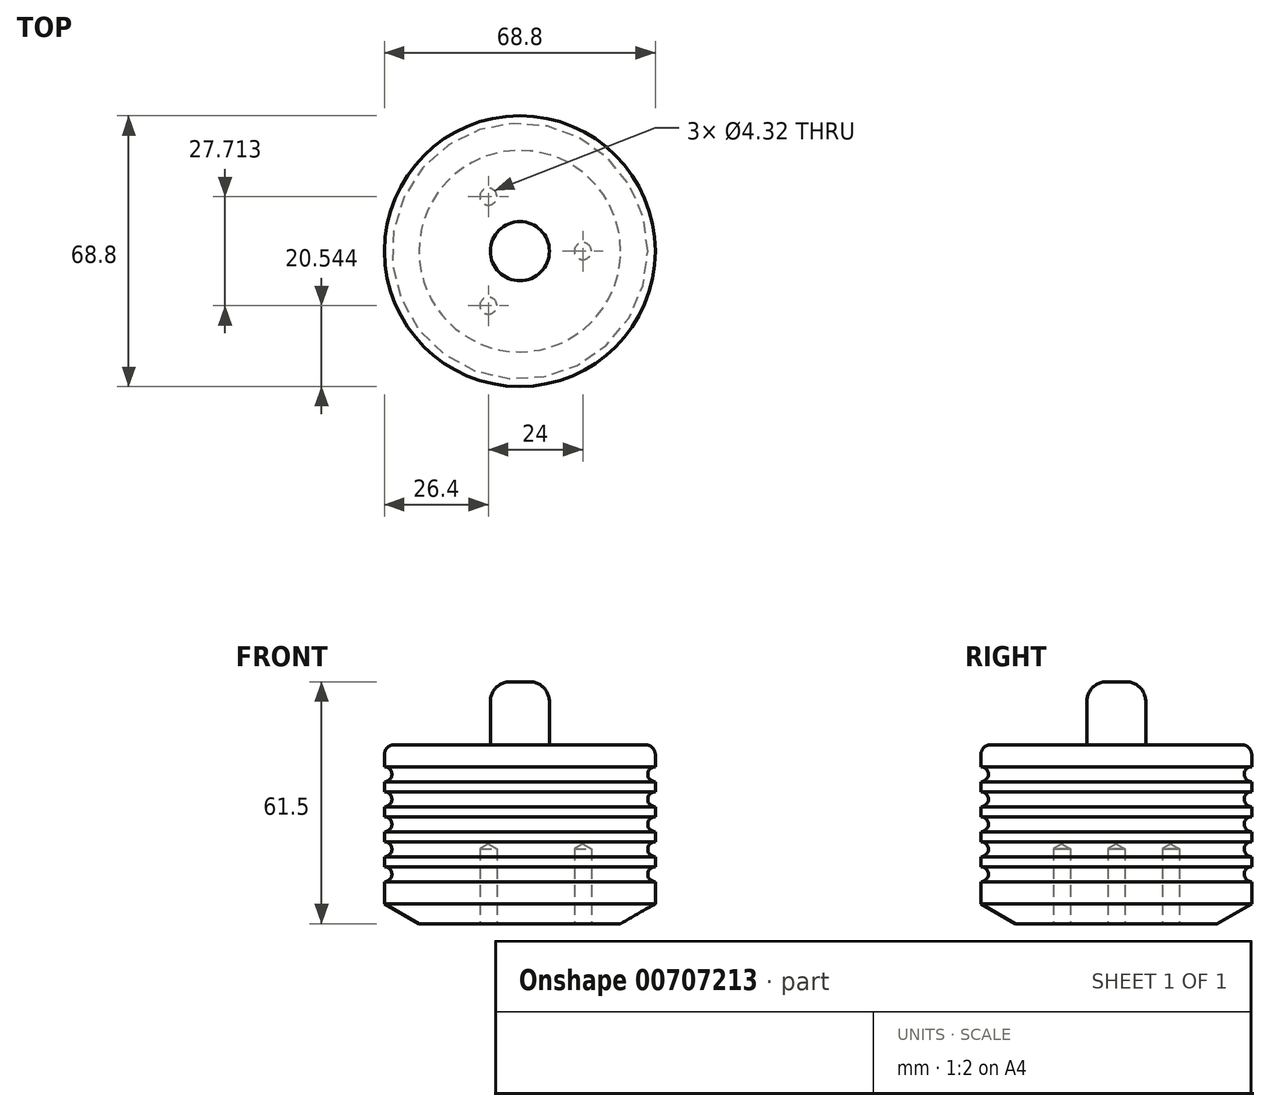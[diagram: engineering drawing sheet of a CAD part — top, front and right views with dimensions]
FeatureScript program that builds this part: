
annotation { "Feature Type Name" : "Feature", "Feature Type Description" : "" }
export const myFeature = defineFeature(function(context is Context, id is Id, definition is map)
    precondition{}
    {
        {
            var Q0;
            Q0=qCreatedBy(makeId("Top.planeOp"),FACE);
            var sketch = newSketch(context, id + "F0", { "sketchPlane" : qUnion([Q0])});
            skCircle(sketch, "E0", {"center": v(0, 0) * mm, "radius": 34.4 * mm});
            skSolve(sketch);
        }
        {
            var Q0;
            Q0 = qSketchRegion(id + "F0", true);
            extrude(context, id + "F1", {"entities" : qUnion([Q0]), "depth" : 45.5 * mm, "offsetDistance" : 25.4 * mm});
        }
        {
            var Q0;
            Q0=makeQuery(id+"F1.opExtrude","CAP_FACE",FACE,{"disambiguationData":[OSD([sQuery(id+"F0.wireOp",EDGE,"E0")])],"isStart":false});
            var sketch = newSketch(context, id + "F2", { "sketchPlane" : qUnion([Q0])});
            skCircle(sketch, "E1", {"center": v(0, 0) * mm, "radius": 7.5 * mm});
            skSolve(sketch);
        }
        {
            var Q0;
            Q0 = qSketchRegion(id + "F2", true);
            extrude(context, id + "F3", {"entities" : qUnion([Q0]), "operationType" : NewBodyOperationType.ADD, "depth" : 16 * mm, "offsetDistance" : 25.4 * mm});
        }
        {
            var Q0;
            Q0=makeQuery(id+"F1.opExtrude","CAP_FACE",FACE,{"disambiguationData":[OSD([sQuery(id+"F0.wireOp",EDGE,"E0")])],"isStart":true});
            var sketch = newSketch(context, id + "F4", { "sketchPlane" : qUnion([Q0])});
            skCircle(sketch, "E2", {"center": v(0, 0) * mm, "radius": 16 * mm});
            skLineSegment(sketch, "E3", {"start": v(0, 0) * mm, "end": v(16, 0) * mm});
            skLineSegment(sketch, "E4", {"start": v(0, 0) * mm, "end": v(-8, 13.86) * mm});
            skLineSegment(sketch, "E5.MirrorCS", {"start": v(0, 0) * mm, "end": v(-8, -13.86) * mm});
            skSolve(sketch);
        }
        {
            var Q0;
            Q0=sQuery(id+"F4.wireOp",VERTEX,"E4.end");
            var Q1;
            Q1=sQuery(id+"F4.wireOp",VERTEX,"E3.end");
            var Q2;
            Q2=sQuery(id+"F4.wireOp",VERTEX,"E5.MirrorCS.end");
            var Q3;
            Q3=makeQuery(id+"F1.opExtrude","SWEPT_BODY",BODY,{"disambiguationData":[OSD([sQuery(id+"F0.wireOp",EDGE,"E0")])]});
            hole(context, id + "F5", {"style" : HoleStyle.SIMPLE, "endStyle" : HoleEndStyle.BLIND, "standardTappedOrClearance" : lookupTablePath({ "standard" : "ANSI", "fit" : "Close", "size" : "#8", "type" : "Clearance" }), "standardBlindInLast" : lookupTablePath({ "fit" : "Close", "standard" : "ANSI", "size" : "#8", "type" : "Clearance" }), "holeDiameter" : 4.32 * mm, "majorDiameter" : 6.35 * mm, "holeDepth" : 19.05 * mm, "isTappedThrough" : true, "tappedDepth" : 12.7 * mm, "tapClearance" : 3, "locations" : qUnion([Q0, Q1, Q2]), "scope" : qUnion([Q3])});
        }
        {
            var Q0;
            Q0=makeQuery(id+"F1.opExtrude","CAP_EDGE",EDGE,{"disambiguationData":[OSD([sQuery(id+"F0.wireOp",EDGE,"E0")])],"isStart":true});
            chamfer(context, id + "F6", {"entities" : qUnion([Q0]), "chamferType" : ChamferType.OFFSET_ANGLE, "width" : 5.08 * mm, "oppositeDirection" : false, "angle" : 60 * degree, "tangentPropagation" : true});
        }
        {
            var Q0;
            Q0=qCreatedBy(makeId("Right.planeOp"),FACE);
            var sketch = newSketch(context, id + "F7", { "sketchPlane" : qUnion([Q0])});
            skLineSegment(sketch, "E6", {"start": v(0, 0) * mm, "end": v(0, 5.08) * mm});
            skLineSegment(sketch, "E7", {"start": v(0, 5.08) * mm, "end": v(-34.4, 5.08) * mm});
            skLineSegment(sketch, "E8", {"start": v(-34.4, 5.08) * mm, "end": v(-34.4, 45.5) * mm});
            skLineSegment(sketch, "E9", {"start": v(-34.4, 25.29) * mm, "end": v(-39.91, 25.29) * mm});
            skCircle(sketch, "E10", {"center": v(-34.4, 25.29) * mm, "radius": 1.9 * mm});
            skLineSegment(sketch, "E11", {"start": v(-34.4, 25.29) * mm, "end": v(-34.4, 31.64) * mm});
            skLineSegment(sketch, "E12", {"start": v(-34.4, 31.64) * mm, "end": v(-34.4, 37.99) * mm});
            skCircle(sketch, "E13", {"center": v(-34.4, 31.64) * mm, "radius": 1.9 * mm});
            skCircle(sketch, "E14", {"center": v(-34.4, 37.99) * mm, "radius": 1.9 * mm});
            skCircle(sketch, "E15.MirrorC", {"center": v(-34.4, 12.6) * mm, "radius": 1.9 * mm});
            skCircle(sketch, "E16.MirrorC", {"center": v(-34.4, 18.94) * mm, "radius": 1.9 * mm});
            skLineSegment(sketch, "E17", {"start": v(0, 0) * mm, "end": v(0, 19.05) * mm});
            skSolve(sketch);
        }
        {
            var Q0;
            Q0 = qSketchRegion(id + "F7", true);
            var Q1;
            Q1=sQuery(id+"F7.wireOp",EDGE,"E17");
            revolve(context, id + "F8", {"operationType" : NewBodyOperationType.REMOVE, "surfaceOperationType" : NewSurfaceOperationType.NEW, "entities" : qUnion([Q0]), "axis" : qUnion([Q1]), "revolveType" : RevolveType.FULL, "oppositeDirection" : true});
        }
        {
            var Q0;
            Q0=makeQuery(id+"F1.opExtrude","CAP_EDGE",EDGE,{"disambiguationData":[OSD([sQuery(id+"F0.wireOp",EDGE,"E0")])],"isStart":false});
            fillet(context, id + "F9", {"entities" : qUnion([Q0]), "radius" : 2.54 * mm, "tangentPropagation" : true, "allowEdgeOverflow" : false});
        }
        {
            var Q0;
            Q0=makeQuery(id+"F3.opExtrude","CAP_EDGE",EDGE,{"disambiguationData":[OSD([sQuery(id+"F2.wireOp",EDGE,"E1")])],"isStart":false});
            fillet(context, id + "F10", {"entities" : qUnion([Q0]), "radius" : 5.08 * mm, "tangentPropagation" : true, "allowEdgeOverflow" : false});
        }
    });
